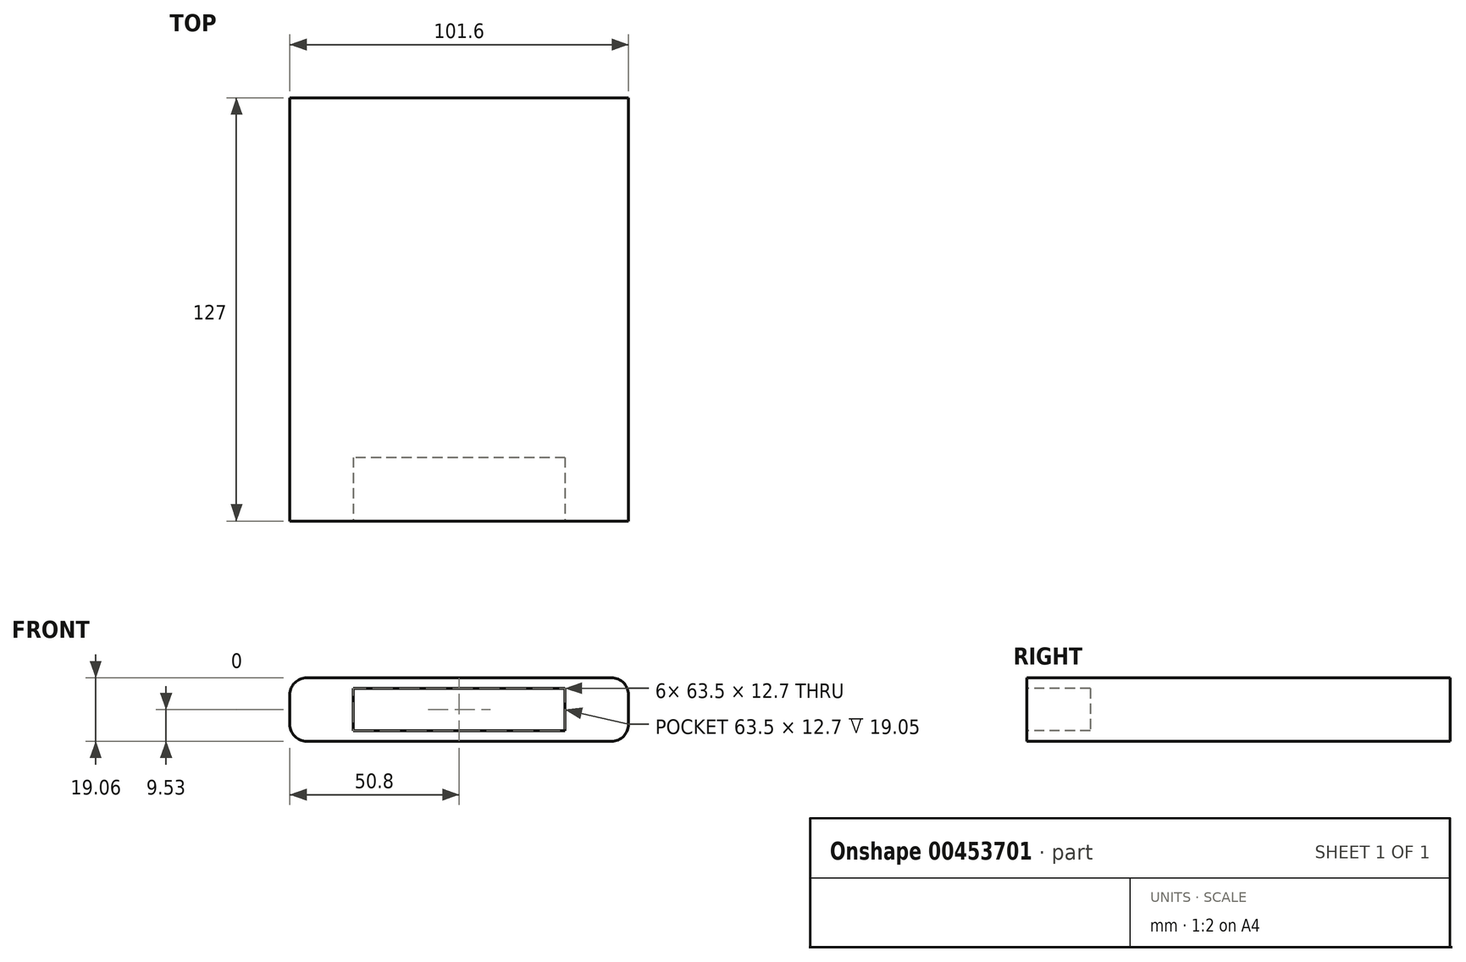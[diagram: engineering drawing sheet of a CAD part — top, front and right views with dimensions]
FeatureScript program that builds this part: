
annotation { "Feature Type Name" : "Feature", "Feature Type Description" : "" }
export const myFeature = defineFeature(function(context is Context, id is Id, definition is map)
    precondition{}
    {
        {
            var Q0;
            Q0=qCreatedBy(makeId("Front.planeOp"),FACE);
            var sketch = newSketch(context, id + "F0", { "sketchPlane" : qUnion([Q0])});
            skLineSegment(sketch, "E0.bottom", {"start": v(50.8, 9.53) * mm, "end": v(-50.8, 9.53) * mm});
            skLineSegment(sketch, "E0.top", {"start": v(50.8, -9.53) * mm, "end": v(-50.8, -9.53) * mm});
            skLineSegment(sketch, "E0.left", {"start": v(50.8, 9.53) * mm, "end": v(50.8, -9.53) * mm});
            skLineSegment(sketch, "E0.right", {"start": v(-50.8, 9.53) * mm, "end": v(-50.8, -9.53) * mm});
            skPoint(sketch, "E0.middle", {"position": v(0, 0) * mm});
            skSolve(sketch);
        }
        {
            var Q0;
            Q0=makeQuery(id+"F0.imprint","IMPRINT",FACE,{"disambiguationData":[TD([[makeQuery(id+"F0.imprint","IMPRINT",EDGE,{"derivedFrom":sQuery(id+"F0.wireOp",EDGE,"E0.bottom")}),1.0]])]});
            var sketch = newSketch(context, id + "F1", { "sketchPlane" : qUnion([Q0])});
            skLineSegment(sketch, "E1.bottom", {"start": v(31.75, 6.35) * mm, "end": v(-31.75, 6.35) * mm});
            skLineSegment(sketch, "E1.top", {"start": v(31.75, -6.35) * mm, "end": v(-31.75, -6.35) * mm});
            skLineSegment(sketch, "E1.left", {"start": v(31.75, 6.35) * mm, "end": v(31.75, -6.35) * mm});
            skLineSegment(sketch, "E1.right", {"start": v(-31.75, 6.35) * mm, "end": v(-31.75, -6.35) * mm});
            skPoint(sketch, "E1.middle", {"position": v(0, 0) * mm});
            skSolve(sketch);
        }
        {
            var Q0;
            Q0 = qSketchRegion(id + "F0", true);
            extrude(context, id + "F2", {"entities" : qUnion([Q0]), "oppositeDirection" : true, "depth" : 127 * mm});
        }
        {
            var Q0;
            Q0 = qSketchRegion(id + "F1", true);
            extrude(context, id + "F3", {"entities" : qUnion([Q0]), "operationType" : NewBodyOperationType.REMOVE, "oppositeDirection" : true, "depth" : 19.05 * mm});
        }
        {
            var Q0;
            Q0=makeQuery(id+"F2.opExtrude","SWEPT_EDGE",EDGE,{"disambiguationData":[OSD([sQuery(id+"F0.wireOp",EDGE,"E0.bottom"),sQuery(id+"F0.wireOp",EDGE,"E0.right")])]});
            var Q1;
            Q1=makeQuery(id+"F2.opExtrude","SWEPT_EDGE",EDGE,{"disambiguationData":[OSD([sQuery(id+"F0.wireOp",EDGE,"E0.bottom"),sQuery(id+"F0.wireOp",EDGE,"E0.left")])]});
            var Q2;
            Q2=makeQuery(id+"F2.opExtrude","SWEPT_EDGE",EDGE,{"disambiguationData":[OSD([sQuery(id+"F0.wireOp",EDGE,"E0.top"),sQuery(id+"F0.wireOp",EDGE,"E0.left")])]});
            var Q3;
            Q3=makeQuery(id+"F2.opExtrude","SWEPT_EDGE",EDGE,{"disambiguationData":[OSD([sQuery(id+"F0.wireOp",EDGE,"E0.top"),sQuery(id+"F0.wireOp",EDGE,"E0.right")])]});
            fillet(context, id + "F4", {"entities" : qUnion([Q0, Q1, Q2, Q3]), "radius" : 5.08 * mm, "tangentPropagation" : true, "allowEdgeOverflow" : false});
        }
    });
